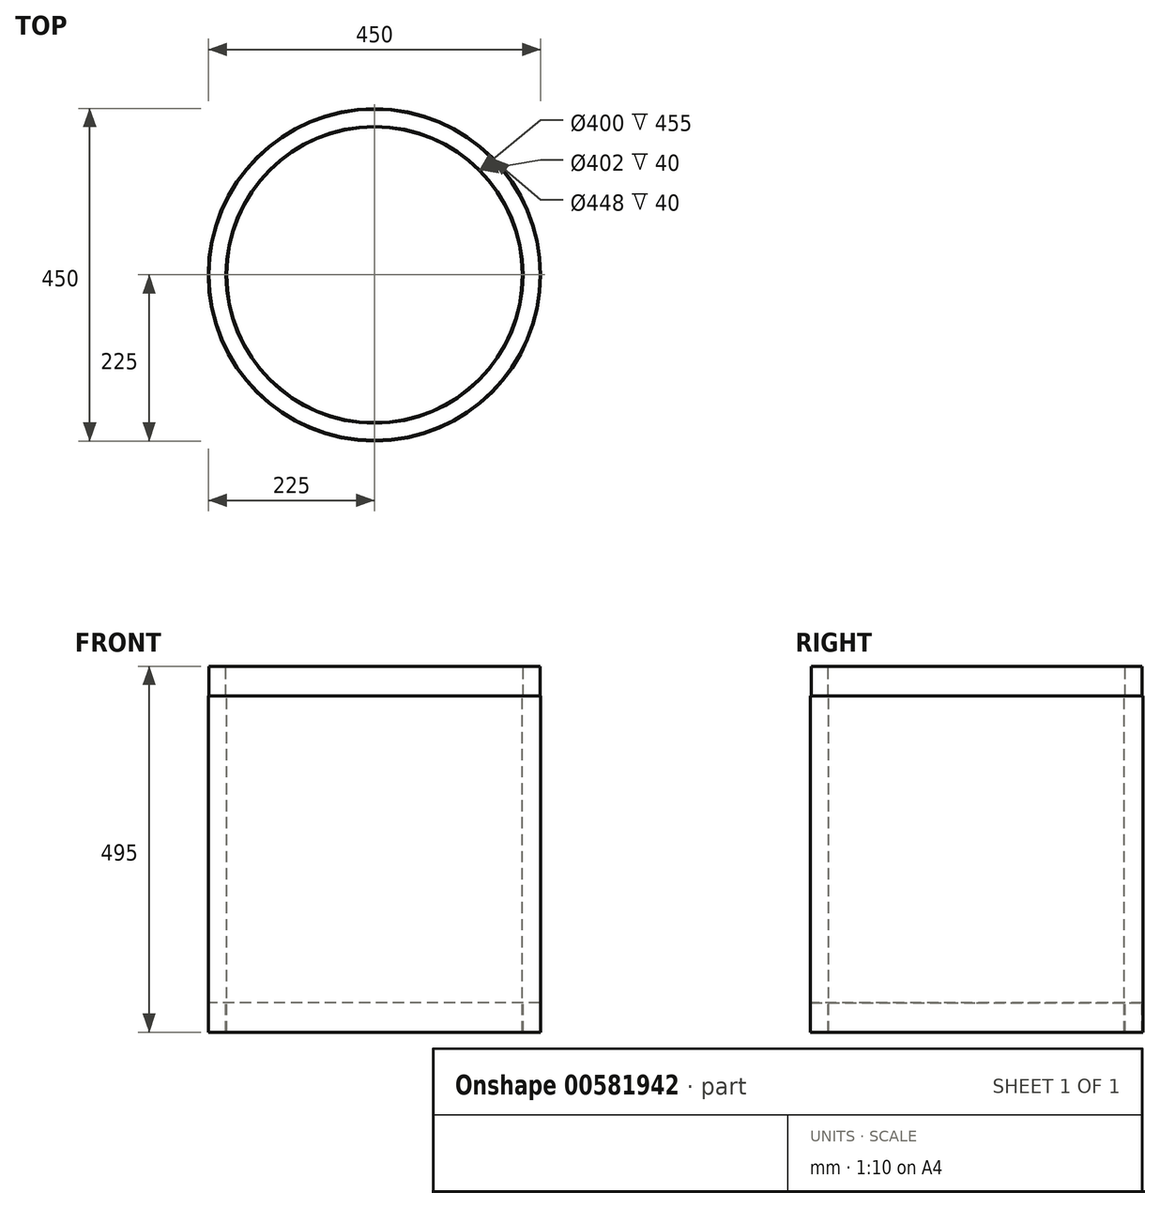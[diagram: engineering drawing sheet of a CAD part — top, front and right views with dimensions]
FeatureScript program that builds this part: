
annotation { "Feature Type Name" : "Feature", "Feature Type Description" : "" }
export const myFeature = defineFeature(function(context is Context, id is Id, definition is map)
    precondition{}
    {
        {
            var Q0;
            Q0=qCreatedBy(makeId("Front.planeOp"),FACE);
            var sketch = newSketch(context, id + "F0", { "sketchPlane" : qUnion([Q0])});
            skLineSegment(sketch, "E0", {"start": v(0, 345.75) * mm, "end": v(0, -558.03) * mm, "construction": true});
            skLineSegment(sketch, "E1", {"start": v(-200, -518.84) * mm, "end": v(-200, -63.84) * mm});
            skLineSegment(sketch, "E2", {"start": v(-200, -63.84) * mm, "end": v(-201, -63.84) * mm});
            skLineSegment(sketch, "E3", {"start": v(-201, -63.84) * mm, "end": v(-201, -23.84) * mm});
            skLineSegment(sketch, "E4", {"start": v(-201, -23.84) * mm, "end": v(-224, -23.84) * mm});
            skLineSegment(sketch, "E5", {"start": v(-224, -23.84) * mm, "end": v(-224, -63.84) * mm});
            skLineSegment(sketch, "E6", {"start": v(-224, -63.84) * mm, "end": v(-225, -63.84) * mm});
            skLineSegment(sketch, "E7", {"start": v(-225, -63.84) * mm, "end": v(-225, -518.84) * mm});
            skLineSegment(sketch, "E8", {"start": v(-225, -518.84) * mm, "end": v(-224, -518.84) * mm});
            skLineSegment(sketch, "E9", {"start": v(-224, -518.84) * mm, "end": v(-224, -478.84) * mm});
            skLineSegment(sketch, "E10", {"start": v(-224, -478.84) * mm, "end": v(-201, -478.84) * mm});
            skLineSegment(sketch, "E11", {"start": v(-201, -478.84) * mm, "end": v(-201, -518.84) * mm});
            skLineSegment(sketch, "E12", {"start": v(-201, -518.84) * mm, "end": v(-200, -518.84) * mm});
            skSolve(sketch);
        }
        {
            var Q0;
            Q0=qSketchRegion(id+"F0",true);
            var Q1;
            Q1=sQuery(id+"F0.wireOp",EDGE,"E0");
            revolve(context, id + "F1", {"entities" : qUnion([Q0]), "axis" : qUnion([Q1]), "revolveType" : RevolveType.FULL});
        }
    });
